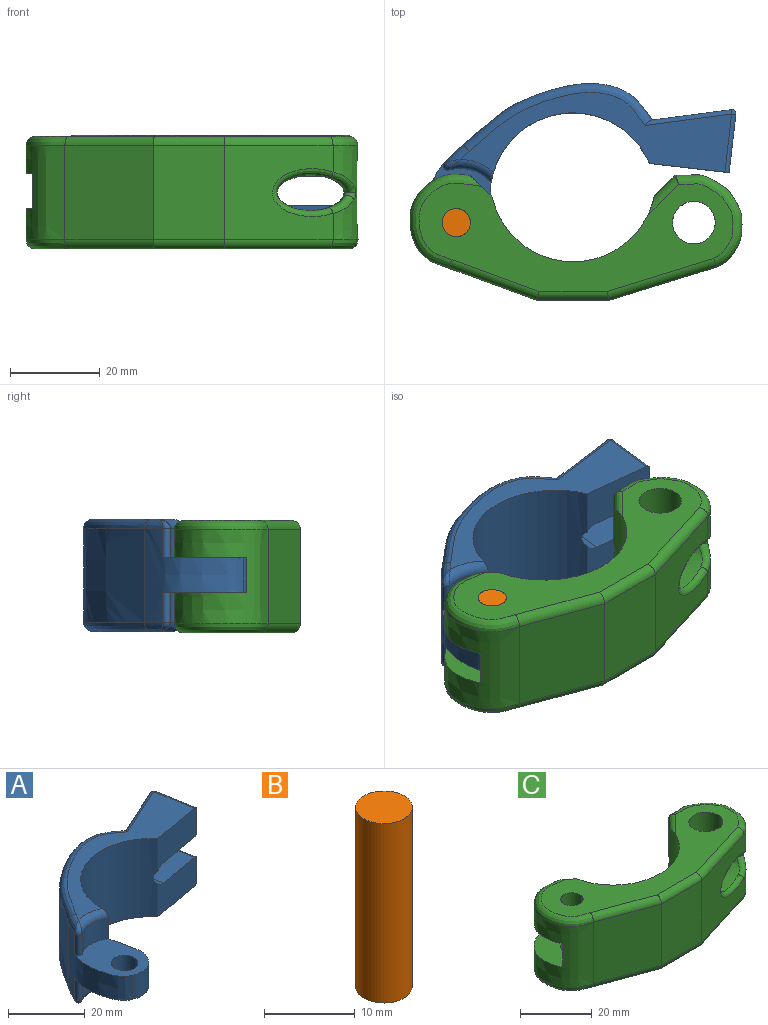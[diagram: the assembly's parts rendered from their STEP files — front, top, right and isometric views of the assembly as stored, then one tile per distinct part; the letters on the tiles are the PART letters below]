
ASSEMBLY  parts=3 mates=2
PART A: 45 faces, bbox 63x48.2x25.6 mm
  f0: plane 12.8x7.32mm, normal (0.98,0.18,0), area 95.2mm2, adj f13,f28,f31,f32
  f1: plane 17.56x10.55mm, normal (0.18,-0.98,0), area 165.7mm2, adj f7,f12,f14,f25,f26,f41,f42
  f2: plane 16.55x10.65mm, normal (-0.41,0.91,0), area 148.2mm2, adj f3,f4,f25,f26,f40,f44
  f3: extruded ~39.77x21.96mm, area 1030.8mm2, adj f2,f4,f5,f8,f24,f25,f35
  f4: bspline ~39.25x23.55mm, area 150.2mm2, adj f2,f3,f7,f20,f40
  f5: bspline ~39.25x23.55mm, area 150.2mm2, adj f3,f11,f22,f24,f29
  f6: plane 7.7x1.53mm, normal (0.95,0.33,0), area 12.4mm2, adj f10,f12,f15,f16
  f7: plane 57.18x27.71mm, normal (0,0,-1), area 398.9mm2, adj f1,f4,f12,f20,f21,f40,f41
  f8: extruded ~22.63x21mm, area 274.3mm2, adj f3,f9,f15,f16,f20,f22,f36,f38
  f9: cylinder r=6.68mm len=9.2mm, axis (0,0,-1), area 111.5mm2, adj f8,f10,f15,f16
  f10: plane 7.7x6mm, normal (0.98,0.18,0), area 47mm2, adj f6,f9,f15,f16
  f11: plane 57.2x27.79mm, normal (0,0,1), area 399.3mm2, adj f5,f12,f13,f22,f23,f28,f29
  f12: cylinder r=18.5mm len=32.68mm, axis (0,0,-1), area 1194.8mm2, adj f1,f6,f7,f11,f13,f15,f16,f18
  f13: plane 17.56x10.55mm, normal (0.18,-0.98,0), area 165.7mm2, adj f0,f11,f12,f25,f27,f28,f31
  f14: plane 12.8x7.32mm, normal (0.98,0.18,0), area 95.2mm2, adj f1,f41,f42,f44
  f15: plane 18.19x14.73mm, normal (0,0,-1), area 175.6mm2, adj f6,f8,f9,f10,f12,f17,f19,f38
  f16: plane 18.17x14.73mm, normal (0,0,1), area 175.1mm2, adj f6,f8,f9,f10,f12,f17,f18,f36
  f17: cylinder r=3.5mm len=7.7mm, axis (0,0,-1), area 169.3mm2, adj f15,f16
  f18: cylinder r=9.17mm len=9.83mm, axis (0,0,1), area 67.9mm2, adj f12,f16,f23,f36
  f19: cylinder r=9.22mm len=9.8mm, axis (0,0,-1), area 69.8mm2, adj f12,f15,f21,f38
  f20: bspline ~7.6x5.32mm, area 13.5mm2, adj f4,f7,f8,f39
  f21: torus R=11.22mm, axis (0,0,1), area 28.6mm2, adj f7,f12,f19,f39
  f22: bspline ~7.44x5.24mm, area 13.6mm2, adj f5,f8,f11,f37
  f23: torus R=11.17mm, axis (0,0,1), area 28.6mm2, adj f11,f12,f18,f37
  f24: plane 16.46x8.51mm, normal (-0.41,0.91,0), area 130.3mm2, adj f3,f5,f29,f32,f34,f35
  f25: cylinder r=3.25mm len=10.82mm, axis (0.18,-0.98,0), area 96.7mm2, adj f1,f2,f3,f12,f13,f26,f27,f35
  f26: plane 16.29x15.9mm, normal (0,0,1), area 174.2mm2, adj f1,f2,f25,f42,f44
  f27: plane 15.72x15.34mm, normal (0,0,-1), area 160mm2, adj f13,f25,f31,f34
  f28: cylinder r=0.97mm len=12.97mm, axis (0.18,-0.98,0), area 19.7mm2, adj f0,f11,f13,f30
  f29: cylinder r=0.97mm len=18.07mm, axis (0.91,0.41,0), area 28.3mm2, adj f5,f11,f24,f30
  f30: sphere r=0.97mm, area 1.1mm2, adj f28,f29,f32
  f31: cylinder r=0.97mm len=12.97mm, axis (0.18,-0.98,0), area 19.7mm2, adj f0,f13,f27,f33
  f32: cylinder r=0.97mm len=7.32mm, axis (0,0,-1), area 12.8mm2, adj f0,f24,f30,f33
  f33: sphere r=0.97mm, area 1.1mm2, adj f31,f32,f34
  f34: cylinder r=0.97mm len=13.81mm, axis (-0.91,-0.41,0), area 22.3mm2, adj f24,f27,f33,f35
  f35: bspline ~4.17x2.52mm, area 4.8mm2, adj f3,f24,f25,f34
  f36: cylinder r=0.97mm len=6.55mm, axis (0,0,-1), area 16.3mm2, adj f8,f16,f18,f37
  f37: bspline ~4.78x4.58mm, area 5mm2, adj f22,f23,f36
  f38: cylinder r=0.97mm len=6.75mm, axis (0,0,-1), area 16.8mm2, adj f8,f15,f19,f39
  f39: bspline ~4.81x4.6mm, area 4.9mm2, adj f20,f21,f38
  f40: cylinder r=0.97mm len=18.07mm, axis (-0.91,-0.41,0), area 28.3mm2, adj f2,f4,f7,f43
  f41: cylinder r=0.97mm len=12.97mm, axis (-0.18,0.98,0), area 19.7mm2, adj f1,f7,f14,f43
  f42: cylinder r=0.97mm len=13.92mm, axis (-0.18,0.98,0), area 20.5mm2, adj f1,f14,f26,f44
  f43: sphere r=0.97mm, area 1.1mm2, adj f40,f41,f44
  f44: cylinder r=0.97mm len=8.28mm, axis (0,0,-1), area 14mm2, adj f2,f14,f26,f42,f43
PART B: 3 faces, bbox 6.3x6.3x24.3 mm
  f0: cylinder r=3.12mm len=24.25mm, axis (0,0,-1), area 476.1mm2, adj f1,f2
  f1: plane 6.25x6.25mm, normal (0,0,1), area 30.7mm2, adj f0
  f2: plane 6.25x6.25mm, normal (0,0,-1), area 30.7mm2, adj f0
PART C: 54 faces, bbox 74.9x31.6x25.9 mm
  f0: plane 69.92x24.1mm, normal (0,0,-1), area 687.4mm2, adj f9,f13,f15,f40,f41,f42,f43,f44
  f1: cylinder r=3.12mm len=6.25mm, axis (0,0,1), area 65.9mm2, adj f20,f47
  f2: bspline ~7.47x2.96mm, area 3.8mm2, adj f3,f7,f22,f29
  f3: bspline ~7.47x2.96mm, area 3.9mm2, adj f2,f4,f7,f22
  f4: bspline ~6.49x6.25mm, area 17.8mm2, adj f3,f6,f7,f22,f30
  f5: plane 7.62x4.44mm, normal (-0.71,0.71,0), area 38.9mm2, adj f13,f23,f24,f39
  f6: plane 24.11x21.01mm, normal (0.3,-0.95,0), area 402.6mm2, adj f4,f7,f17,f29,f30,f36,f43
  f7: extruded ~21x20.45mm, area 536.4mm2, adj f2,f3,f4,f6,f24,f25,f26,f27
  f8: plane 7.62x4.45mm, normal (-0.71,0.71,0), area 38.9mm2, adj f13,f23,f28,f46
  f9: cylinder r=4.75mm len=9.5mm, axis (0,0,1), area 234.1mm2, adj f0,f31
  f10: cylinder r=4.75mm len=9.5mm, axis (0,0,1), area 234mm2, adj f18,f32
  f11: plane 9.07x5.8mm, normal (0.68,0.73,0), area 52.6mm2, adj f12,f13,f18,f19,f33
  f12: extruded ~21x20.9mm, area 517.1mm2, adj f11,f15,f16,f19,f20,f21,f33,f40
  f13: cylinder r=18.5mm len=36.19mm, axis (0,0,-1), area 1140.6mm2, adj f0,f5,f8,f11,f15,f18,f19,f20
  f14: cylinder r=3.12mm len=8.14mm, axis (0,0,1), area 159.9mm2, adj f18,f19
  f15: plane 9.78x5.79mm, normal (0.68,0.73,0), area 57.4mm2, adj f0,f12,f13,f20,f40
  f16: plane 21x19.64mm, normal (-0.34,-0.94,0), area 439.3mm2, adj f12,f17,f34,f41
  f17: plane 21x15.94mm, normal (0,-1,0), area 334.6mm2, adj f6,f16,f35,f42
  f18: plane 69.92x24.1mm, normal (0,0,1), area 763.4mm2, adj f10,f11,f13,f14,f33,f34,f35,f36
  f19: plane 25.67x16.2mm, normal (0,0,-1), area 253.7mm2, adj f11,f12,f13,f14,f21
  f20: plane 25.67x16.2mm, normal (0,0,1), area 253.7mm2, adj f1,f12,f13,f15,f21
  f21: plane 24.16x8mm, normal (0,1,0), area 193.3mm2, adj f12,f13,f19,f20
  f22: extruded ~22.88x14.96mm, area 429.3mm2, adj f2,f3,f4,f23,f26,f29,f30,f31
  f23: bspline ~10.97x9.72mm, area 56.2mm2, adj f5,f8,f13,f22,f25,f27
  f24: cylinder r=0.49mm len=5.33mm, axis (0,0,-1), area 2.1mm2, adj f5,f7,f25,f38
  f25: bspline ~2.72x1.49mm, area 1.3mm2, adj f7,f23,f24,f26
  f26: bspline ~12.06x8.97mm, area 23.5mm2, adj f7,f22,f25,f27
  f27: bspline ~2.72x1.72mm, area 1.3mm2, adj f7,f23,f26,f28
  f28: cylinder r=0.49mm len=5.33mm, axis (0,0,-1), area 2.1mm2, adj f7,f8,f27,f45
  f29: bspline ~6.63x6.58mm, area 17.9mm2, adj f2,f6,f7,f22,f30
  f30: bspline ~14.11x10.68mm, area 60mm2, adj f4,f6,f22,f29
  f31: bspline ~12.19x10.88mm, area 57.8mm2, adj f9,f22
  f32: bspline ~12.19x10.88mm, area 57.8mm2, adj f10,f22
  f33: bspline ~22.88x19.45mm, area 105.4mm2, adj f11,f12,f18,f34
  f34: cylinder r=2mm len=20.33mm, axis (-0.94,0.34,0), area 65.2mm2, adj f16,f18,f33,f35
  f35: cylinder r=2mm len=15.94mm, axis (-1,0,0), area 49mm2, adj f17,f18,f34,f36
  f36: cylinder r=2mm len=24.7mm, axis (-0.95,-0.3,0), area 78.5mm2, adj f6,f18,f35,f37
  f37: bspline ~21.3x16.2mm, area 95.1mm2, adj f7,f18,f36,f38
  f38: bspline ~2.44x2.02mm, area 0.5mm2, adj f24,f37,f39
  f39: cylinder r=2mm len=8.76mm, axis (0.71,0.71,0), area 25.1mm2, adj f5,f13,f18,f38
  f40: bspline ~22.88x19.45mm, area 105.4mm2, adj f0,f12,f15,f41
  f41: cylinder r=2mm len=20.33mm, axis (0.94,-0.34,0), area 65.2mm2, adj f0,f16,f40,f42
  f42: cylinder r=2mm len=15.94mm, axis (1,0,0), area 49mm2, adj f0,f17,f41,f43
  f43: cylinder r=2mm len=24.7mm, axis (0.95,0.3,0), area 78.5mm2, adj f0,f6,f42,f44
  f44: bspline ~21.3x16.2mm, area 95.1mm2, adj f0,f7,f43,f45
  f45: bspline ~2.44x2.02mm, area 0.5mm2, adj f28,f44,f46
  f46: cylinder r=2mm len=8.76mm, axis (-0.71,-0.71,0), area 25.1mm2, adj f0,f8,f13,f45
  f47: plane 12.48x12.27mm, normal (0,0,-1), area 76mm2, adj f1,f48,f49,f50,f51,f52,f53
  f48: plane 6.24x5.5mm, normal (-0.97,0.23,0), area 35.2mm2, adj f0,f47,f49,f53
  f49: plane 6.14x5.5mm, normal (-0.29,0.96,0), area 35.2mm2, adj f0,f47,f48,f50
  f50: plane 5.5x4.67mm, normal (0.68,0.73,0), area 35.2mm2, adj f0,f47,f49,f51
  f51: plane 6.24x5.5mm, normal (0.97,-0.23,0), area 35.2mm2, adj f0,f47,f50,f52
  f52: plane 6.14x5.5mm, normal (0.29,-0.96,0), area 35.2mm2, adj f0,f47,f51,f53
  f53: plane 5.5x4.67mm, normal (-0.68,-0.73,0), area 35.2mm2, adj f0,f47,f48,f52
PLACE A rot(axis=(0,0,-1),16.9deg) t=(-11.79,1.13,-4.67)mm
PLACE B rot(axis=(0,0,-1),16.9deg) t=(-38.22,-14.71,-4.57)mm
PLACE C t=(-11.66,20.01,-4.95)mm
MATE revolute C.f1 <-> B.f0  axis (0,0,1) through (-38.22,-14.71,7.55)mm
MATE fastened A.f17 <-> B.f0  axis (0,0,-1) through (-38.22,-14.71,-4.57)mm
